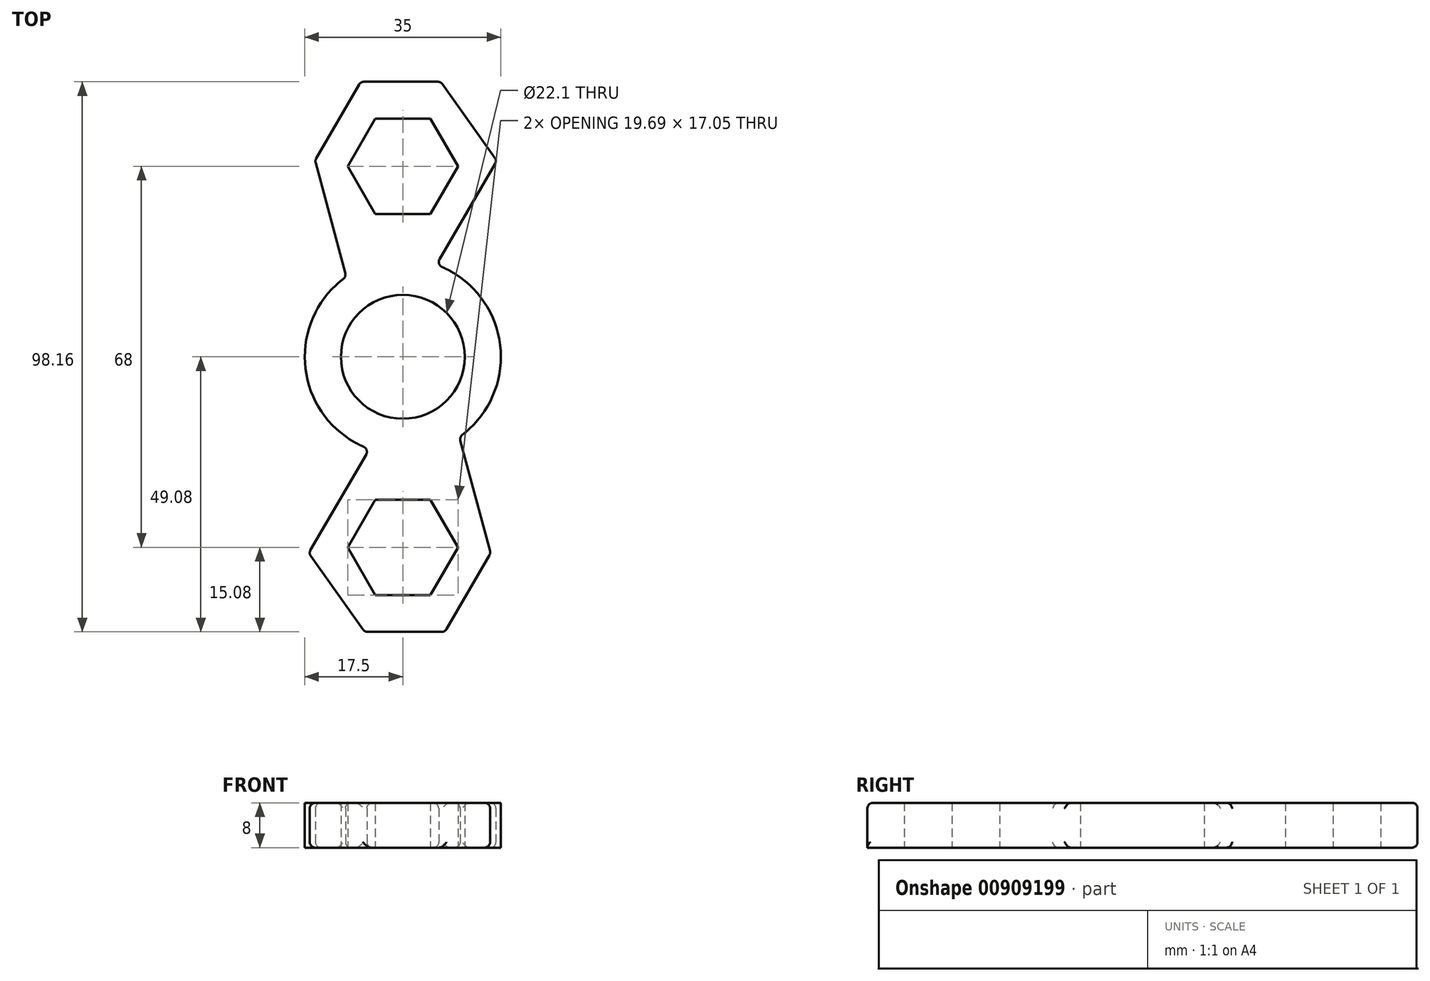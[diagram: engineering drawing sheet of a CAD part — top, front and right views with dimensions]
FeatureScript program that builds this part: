
annotation { "Feature Type Name" : "Feature", "Feature Type Description" : "" }
export const myFeature = defineFeature(function(context is Context, id is Id, definition is map)
    precondition{}
    {
        {
            var Q0;
            Q0=qCreatedBy(makeId("Top.planeOp"),FACE);
            var sketch = newSketch(context, id + "F0", { "sketchPlane" : qUnion([Q0])});
            skCircle(sketch, "E0", {"center": v(0, 0) * mm, "radius": 1.58 * mm});
            skCircle(sketch, "E1", {"center": v(0, 0) * mm, "radius": 11.05 * mm});
            skCircle(sketch, "E2", {"center": v(0, 0) * mm, "radius": 17.5 * mm});
            skLineSegment(sketch, "E3", {"start": v(0, 0) * mm, "end": v(0, 34) * mm, "construction": true});
            skCircle(sketch, "E4.cCircle", {"center": v(0, 34) * mm, "radius": 8.53 * mm, "construction": true});
            skLineSegment(sketch, "E4.0", {"start": v(4.92, 42.53) * mm, "end": v(9.84, 34) * mm});
            skLineSegment(sketch, "E4.1", {"start": v(9.84, 34) * mm, "end": v(4.92, 25.47) * mm});
            skLineSegment(sketch, "E4.2", {"start": v(4.92, 25.47) * mm, "end": v(-4.92, 25.47) * mm});
            skLineSegment(sketch, "E4.3", {"start": v(-4.92, 25.47) * mm, "end": v(-9.84, 34) * mm});
            skLineSegment(sketch, "E4.4", {"start": v(-9.84, 34) * mm, "end": v(-4.92, 42.53) * mm});
            skLineSegment(sketch, "E4.5", {"start": v(-4.92, 42.53) * mm, "end": v(4.92, 42.53) * mm});
            skPoint(sketch, "E4.0.midPoint", {"position": v(7.38, 38.26) * mm});
            skLineSegment(sketch, "E5", {"start": v(0, 0) * mm, "end": v(34, 0) * mm});
            skLineSegment(sketch, "E6", {"start": v(-10.1, 14.3) * mm, "end": v(-15.67, 35.04) * mm});
            skLineSegment(sketch, "E7", {"start": v(-15.67, 35.04) * mm, "end": v(-7.5, 49.08) * mm});
            skLineSegment(sketch, "E8", {"start": v(-7.5, 49.08) * mm, "end": v(6.8, 49.08) * mm});
            skLineSegment(sketch, "E9", {"start": v(6.8, 49.08) * mm, "end": v(16.8, 35.03) * mm});
            skLineSegment(sketch, "E10", {"start": v(16.8, 35.03) * mm, "end": v(11.8, 26.45) * mm});
            skLineSegment(sketch, "E11", {"start": v(11.8, 26.45) * mm, "end": v(5.96, 16.45) * mm});
            skSolve(sketch);
        }
        {
            var Q0;
            Q0=makeQuery(id+"F0.imprint","IMPRINT",FACE,{"disambiguationData":[TD([[makeQuery(id+"F0.imprint","IMPRINT",EDGE,{"derivedFrom":sQuery(id+"F0.wireOp",EDGE,"E1")}),-1.0]])]});
            var Q1;
            Q1=makeQuery(id+"F0.imprint","IMPRINT",FACE,{"disambiguationData":[TD([[makeQuery(id+"F0.imprint","IMPRINT",EDGE,{"derivedFrom":sQuery(id+"F0.wireOp",EDGE,"E4.0")}),1.0]])]});
            extrude(context, id + "F1", {"entities" : qUnion([Q0, Q1]), "depth" : 8 * mm, "offsetDistance" : 25 * mm});
        }
        {
            var Q0;
            Q0=makeQuery(id+"F1.opExtrude","SWEPT_BODY",BODY,{"disambiguationData":[OSD([sQuery(id+"F0.wireOp",EDGE,"E1"),sQuery(id+"F0.wireOp",EDGE,"E2"),sQuery(id+"F0.wireOp",EDGE,"E4.0"),sQuery(id+"F0.wireOp",EDGE,"E4.1"),sQuery(id+"F0.wireOp",EDGE,"E4.2"),sQuery(id+"F0.wireOp",EDGE,"E4.3"),sQuery(id+"F0.wireOp",EDGE,"E4.4"),sQuery(id+"F0.wireOp",EDGE,"E4.5"),sQuery(id+"F0.wireOp",EDGE,"E6"),sQuery(id+"F0.wireOp",EDGE,"E7"),sQuery(id+"F0.wireOp",EDGE,"E8"),sQuery(id+"F0.wireOp",EDGE,"E9"),sQuery(id+"F0.wireOp",EDGE,"E10"),sQuery(id+"F0.wireOp",EDGE,"E11")])]});
            var Q1;
            Q1=makeQuery(id+"F1.opExtrude","CAP_EDGE",EDGE,{"disambiguationData":[OSD([sQuery(id+"F0.wireOp",EDGE,"E1")])],"isStart":true});
            circularPattern(context, id + "F2", {"operationType" : NewBodyOperationType.ADD, "entities" : qUnion([Q0]), "axis" : qUnion([Q1]), "angle" : 360 * degree, "instanceCount" : 2, "equalSpace" : true});
        }
        {
            var Q0;
            Q0=makeQuery(id+"F2.opPattern","COPY",FACE,{"derivedFrom":makeQuery(id+"F1.opExtrude","SWEPT_FACE",FACE,{"disambiguationData":[OSD([sQuery(id+"F0.wireOp",EDGE,"E7")])]}),"instanceName":"1"});
            var Q1;
            Q1=makeQuery(id+"F2.opPattern","COPY",FACE,{"derivedFrom":makeQuery(id+"F1.opExtrude","SWEPT_FACE",FACE,{"disambiguationData":[OSD([sQuery(id+"F0.wireOp",EDGE,"E6")])]}),"instanceName":"1"});
            var Q2;
            Q2=makeQuery(id+"F1.opExtrude","SWEPT_FACE",FACE,{"disambiguationData":[OSD([sQuery(id+"F0.wireOp",EDGE,"E10"),sQuery(id+"F0.wireOp",EDGE,"E11")])]});
            var Q3;
            Q3=makeQuery(id+"F1.opExtrude","SWEPT_FACE",FACE,{"disambiguationData":[OSD([sQuery(id+"F0.wireOp",EDGE,"E9")])]});
            var Q4;
            Q4=makeQuery(id+"F1.opExtrude","SWEPT_FACE",FACE,{"disambiguationData":[OSD([sQuery(id+"F0.wireOp",EDGE,"E8")])]});
            var Q5;
            Q5=makeQuery(id+"F1.opExtrude","SWEPT_FACE",FACE,{"disambiguationData":[OSD([sQuery(id+"F0.wireOp",EDGE,"E7")])]});
            var Q6;
            Q6=makeQuery(id+"F1.opExtrude","SWEPT_FACE",FACE,{"disambiguationData":[OSD([sQuery(id+"F0.wireOp",EDGE,"E6")])]});
            var Q7;
            Q7=makeQuery(id+"F2.opPattern","COPY",FACE,{"derivedFrom":makeQuery(id+"F1.opExtrude","SWEPT_FACE",FACE,{"disambiguationData":[OSD([sQuery(id+"F0.wireOp",EDGE,"E10"),sQuery(id+"F0.wireOp",EDGE,"E11")])]}),"instanceName":"1"});
            var Q8;
            Q8=makeQuery(id+"F2.opPattern","COPY",FACE,{"derivedFrom":makeQuery(id+"F1.opExtrude","SWEPT_FACE",FACE,{"disambiguationData":[OSD([sQuery(id+"F0.wireOp",EDGE,"E9")])]}),"instanceName":"1"});
            var Q9;
            Q9=makeQuery(id+"F2.opPattern","COPY",EDGE,{"derivedFrom":makeQuery(id+"F1.opExtrude","CAP_EDGE",EDGE,{"disambiguationData":[OSD([sQuery(id+"F0.wireOp",EDGE,"E8")])],"isStart":false}),"instanceName":"1"});
            fillet(context, id + "F3", {"entities" : qUnion([Q0, Q1, Q2, Q3, Q4, Q5, Q6, Q7, Q8, Q9]), "radius" : 1 * mm, "tangentPropagation" : true, "allowEdgeOverflow" : false});
        }
    });
